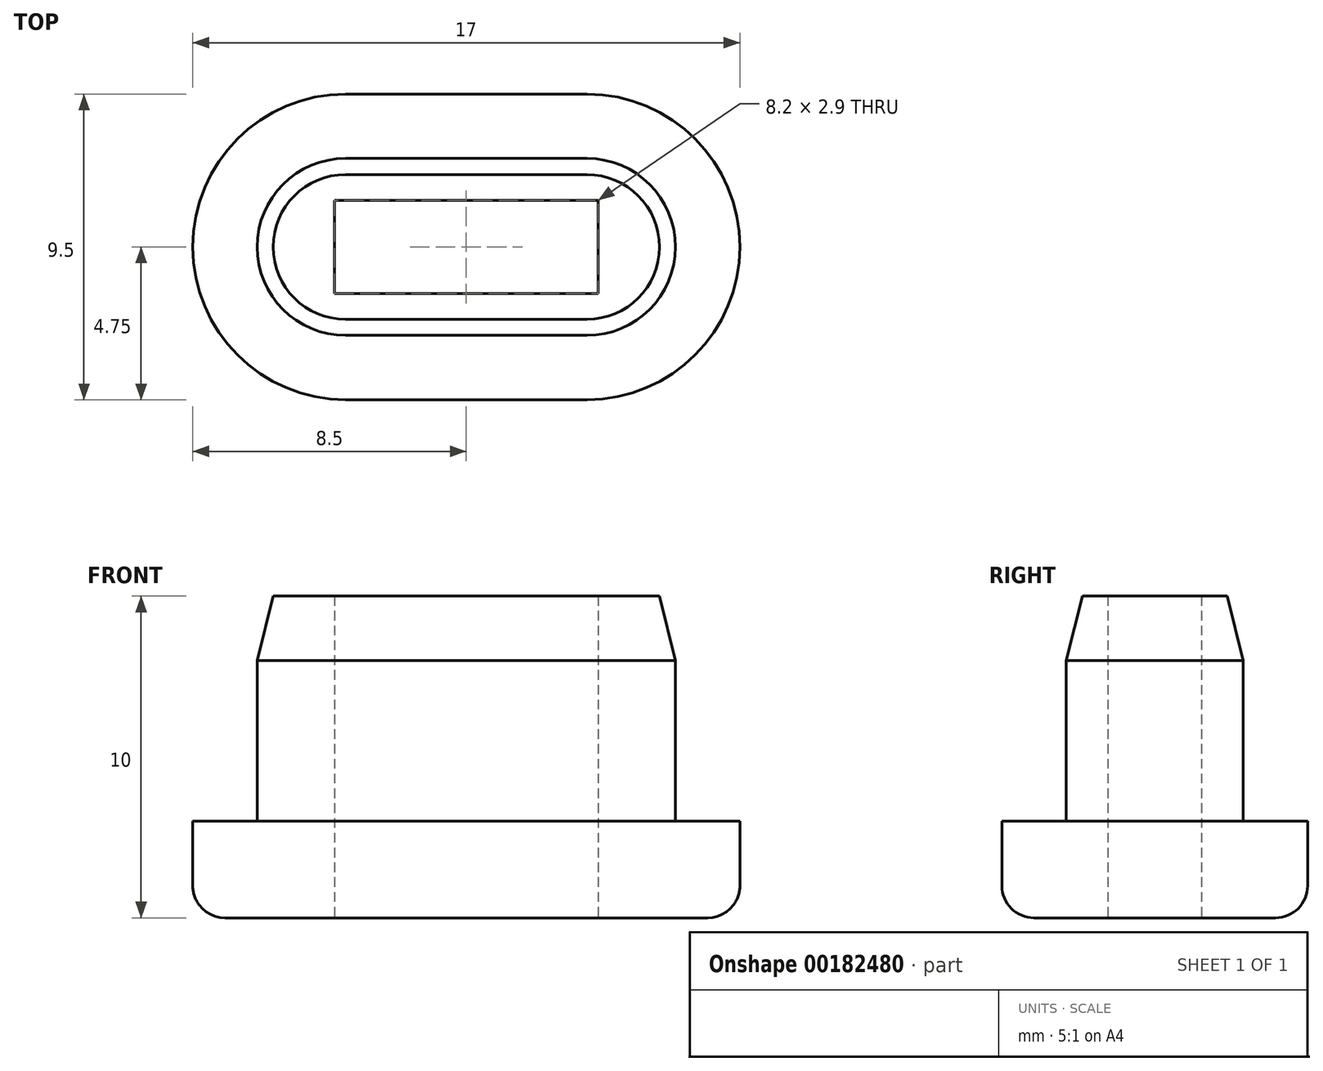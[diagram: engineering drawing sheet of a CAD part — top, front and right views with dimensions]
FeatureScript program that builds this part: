
annotation { "Feature Type Name" : "Feature", "Feature Type Description" : "" }
export const myFeature = defineFeature(function(context is Context, id is Id, definition is map)
    precondition{}
    {
        {
            var Q0;
            Q0=qCreatedBy(makeId("Top.planeOp"),FACE);
            var sketch = newSketch(context, id + "F0", { "sketchPlane" : qUnion([Q0])});
            skLineSegment(sketch, "E0", {"start": v(-3.75, 0) * mm, "end": v(3.75, 0) * mm, "construction": true});
            skCircle(sketch, "E1", {"center": v(-3.75, 0) * mm, "radius": 2.75 * mm});
            skCircle(sketch, "E2", {"center": v(3.75, 0) * mm, "radius": 2.75 * mm});
            skLineSegment(sketch, "E3", {"start": v(-3.75, 2.75) * mm, "end": v(3.75, 2.75) * mm});
            skLineSegment(sketch, "E4", {"start": v(3.75, -2.75) * mm, "end": v(-3.75, -2.75) * mm});
            skLineSegment(sketch, "E5.bottom", {"start": v(-4.1, 1.45) * mm, "end": v(4.1, 1.45) * mm});
            skLineSegment(sketch, "E5.top", {"start": v(-4.1, -1.45) * mm, "end": v(4.1, -1.45) * mm});
            skLineSegment(sketch, "E5.left", {"start": v(-4.1, 1.45) * mm, "end": v(-4.1, -1.45) * mm});
            skLineSegment(sketch, "E5.right", {"start": v(4.1, 1.45) * mm, "end": v(4.1, -1.45) * mm});
            skPoint(sketch, "E5.middle", {"position": v(0, 0) * mm});
            skSolve(sketch);
        }
        {
            var Q0;
            {var subQ0=sQuery(id+"F0.wireOp",EDGE,"E3");Q0=makeQuery(id+"F0.imprint","IMPRINT",FACE,{"disambiguationData":[TD([[makeQuery(id+"F0.imprint","IMPRINT",EDGE,{"derivedFrom":subQ0}),-1.0]])]});}
            var Q1;
            {var subQ6=sQuery(id+"F0.wireOp",EDGE,"E5.left");Q1=makeQuery(id+"F0.imprint","IMPRINT",FACE,{"disambiguationData":[TD([[makeQuery(id+"F0.imprint","IMPRINT",EDGE,{"derivedFrom":subQ6}),-1.0]])]});}
            var Q2;
            {var subQ0=sQuery(id+"F0.wireOp",EDGE,"E5.right");Q2=makeQuery(id+"F0.imprint","IMPRINT",FACE,{"disambiguationData":[TD([[makeQuery(id+"F0.imprint","IMPRINT",EDGE,{"derivedFrom":subQ0}),1.0]])]});}
            var Q3;
            {var subQ0=sQuery(id+"F0.wireOp",EDGE,"E4");Q3=makeQuery(id+"F0.imprint","IMPRINT",FACE,{"disambiguationData":[TD([[makeQuery(id+"F0.imprint","IMPRINT",EDGE,{"derivedFrom":subQ0}),-1.0]])]});}
            extrude(context, id + "F1", {"entities" : qUnion([Q0, Q1, Q2, Q3]), "depth" : 10 * mm, "offsetDistance" : 25 * mm});
        }
        {
            var Q0;
            Q0=makeQuery(id+"F1.opExtrude","CAP_EDGE",EDGE,{"disambiguationData":[OSD([sQuery(id+"F0.wireOp",EDGE,"E4")])],"isStart":false});
            chamfer(context, id + "F2", {"entities" : qUnion([Q0]), "chamferType" : ChamferType.TWO_OFFSETS, "width1" : 2 * mm, "oppositeDirection" : false, "width2" : 0.5 * mm, "tangentPropagation" : true});
        }
        {
            var Q0;
            Q0=makeQuery(id+"F1.opExtrude","CAP_FACE",FACE,{"disambiguationData":[OSD([sQuery(id+"F0.wireOp",EDGE,"E1"),sQuery(id+"F0.wireOp",EDGE,"E2"),sQuery(id+"F0.wireOp",EDGE,"E3"),sQuery(id+"F0.wireOp",EDGE,"E4"),sQuery(id+"F0.wireOp",EDGE,"E5.bottom"),sQuery(id+"F0.wireOp",EDGE,"E5.top"),sQuery(id+"F0.wireOp",EDGE,"E5.left"),sQuery(id+"F0.wireOp",EDGE,"E5.right")])],"isStart":true});
            var sketch = newSketch(context, id + "F3", { "sketchPlane" : qUnion([Q0])});
            skLineSegment(sketch, "E6.0", {"start": v(3.75, 4.75) * mm, "end": v(-3.75, 4.75) * mm});
            skArc(sketch, "E6.1", {"start": v(3.75, 4.75) * mm, "mid": v(8.5, 0) * mm, "end": v(3.75, -4.75) * mm});
            skLineSegment(sketch, "E6.2", {"start": v(-3.75, -4.75) * mm, "end": v(3.75, -4.75) * mm});
            skArc(sketch, "E6.3", {"start": v(-3.75, -4.75) * mm, "mid": v(-8.5, 0) * mm, "end": v(-3.75, 4.75) * mm});
            skSolve(sketch);
        }
        {
            var Q0;
            Q0=makeQuery(id+"F3.imprint","IMPRINT",FACE,{"disambiguationData":[TD([[makeQuery(id+"F3.imprint","IMPRINT",EDGE,{"derivedFrom":sQuery(id+"F3.wireOp",EDGE,"E6.0")}),1.0]])]});
            extrude(context, id + "F4", {"entities" : qUnion([Q0]), "operationType" : NewBodyOperationType.ADD, "oppositeDirection" : true, "depth" : 3 * mm, "offsetDistance" : 25 * mm});
        }
        {
            var Q0;
            Q0=makeQuery(id+"F4.opExtrude","CAP_EDGE",EDGE,{"disambiguationData":[OSD([sQuery(id+"F3.wireOp",EDGE,"E6.0")])],"isStart":true});
            var Q1;
            Q1=makeQuery(id+"F4.opExtrude","CAP_EDGE",EDGE,{"disambiguationData":[OSD([sQuery(id+"F3.wireOp",EDGE,"E6.1")])],"isStart":true});
            var Q2;
            Q2=makeQuery(id+"F4.opExtrude","CAP_EDGE",EDGE,{"disambiguationData":[OSD([sQuery(id+"F3.wireOp",EDGE,"E6.2")])],"isStart":true});
            fillet(context, id + "F5", {"entities" : qUnion([Q0, Q1, Q2]), "tangentPropagation" : true, "radius" : 1 * mm, "defaultsChanged" : true, "vertexSettings" : [], "allowEdgeOverflow" : false});
        }
    });
